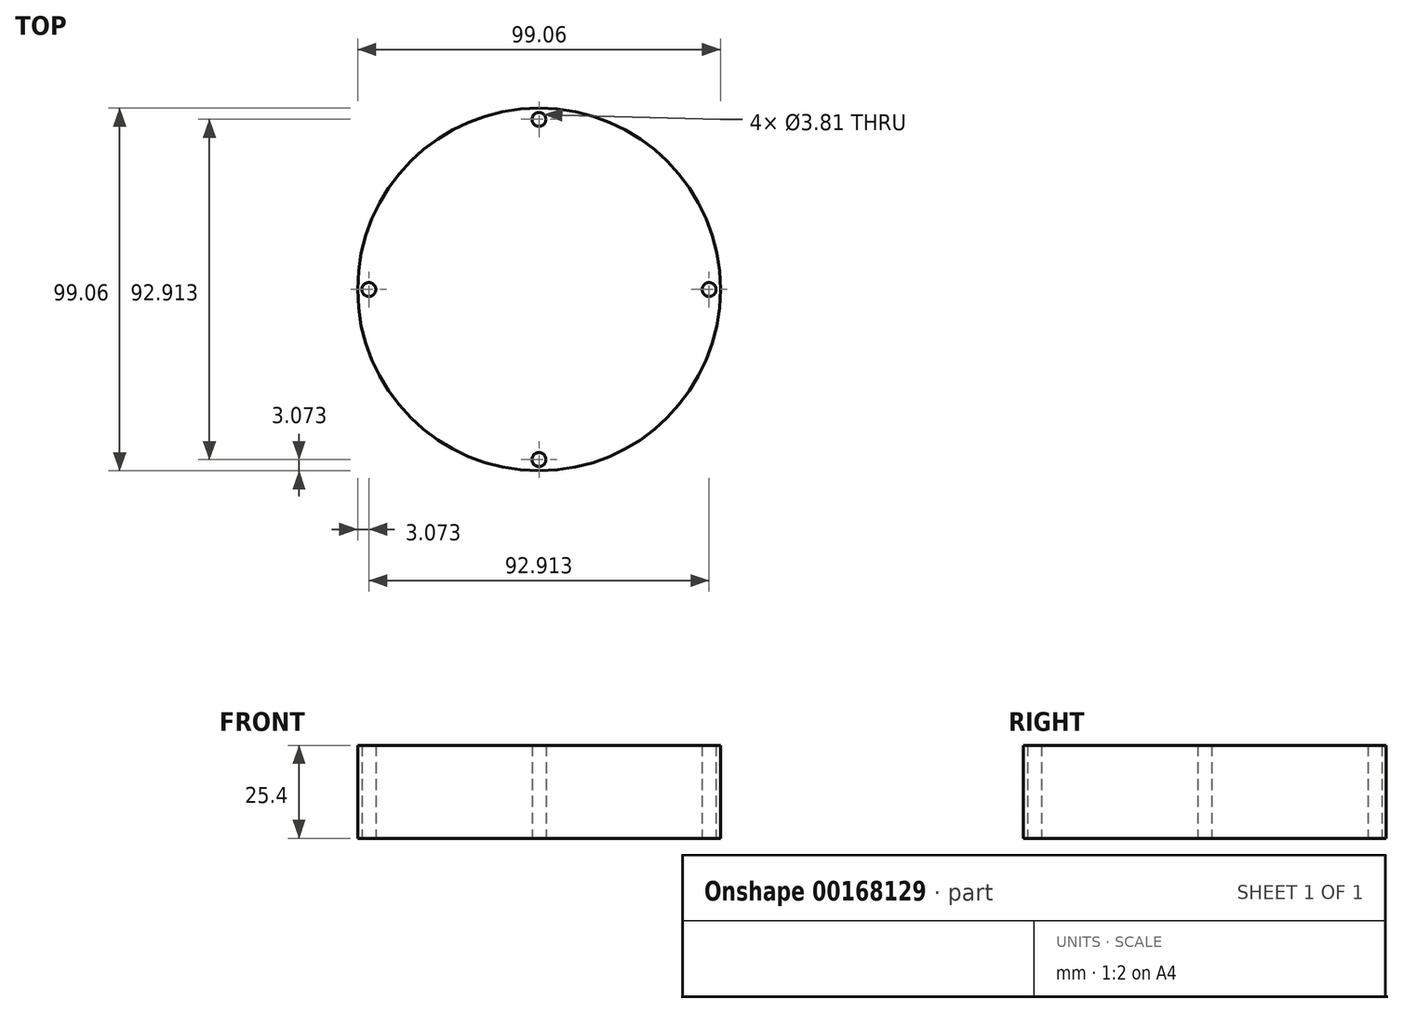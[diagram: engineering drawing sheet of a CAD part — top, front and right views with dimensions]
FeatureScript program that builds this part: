
annotation { "Feature Type Name" : "Feature", "Feature Type Description" : "" }
export const myFeature = defineFeature(function(context is Context, id is Id, definition is map)
    precondition{}
    {
        {
            var Q0;
            Q0=qCreatedBy(makeId("Top.planeOp"),FACE);
            var sketch = newSketch(context, id + "F0", { "sketchPlane" : qUnion([Q0])});
            skCircle(sketch, "E0", {"center": v(0, 0) * mm, "radius": 49.53 * mm});
            skCircle(sketch, "E1", {"center": v(0, 46.46) * mm, "radius": 1.9 * mm});
            skCircle(sketch, "E2.1.0", {"center": v(-46.46, 0) * mm, "radius": 1.9 * mm});
            skCircle(sketch, "E2.2.0", {"center": v(0, -46.46) * mm, "radius": 1.9 * mm});
            skCircle(sketch, "E2.3.0", {"center": v(46.46, 0) * mm, "radius": 1.9 * mm});
            skSolve(sketch);
        }
        {
            var Q0;
            Q0 = qSketchRegion(id + "F0", true);
            extrude(context, id + "F1", {"entities" : qUnion([Q0]), "depth" : 25.4 * mm});
        }
    });
